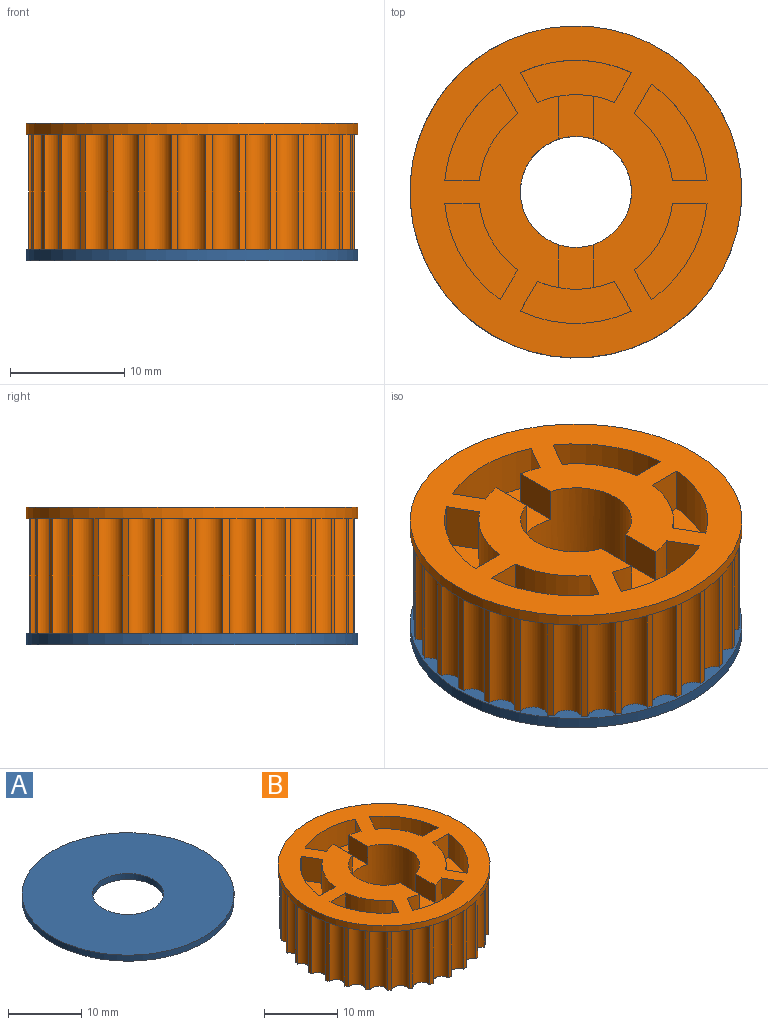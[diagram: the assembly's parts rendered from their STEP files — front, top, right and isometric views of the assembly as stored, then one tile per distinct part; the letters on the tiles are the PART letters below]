
ASSEMBLY  parts=2 mates=1
PART A: 4 faces, bbox 29x29x1 mm
  f0: cylinder r=14.5mm len=29mm, axis (0,0,-1), area 91.1mm2, adj f1,f2
  f1: plane 29x29mm, normal (0,0,1), area 586.6mm2, adj f0,f3
  f2: plane 29x29mm, normal (0,0,-1), area 586.6mm2, adj f0,f3
  f3: cylinder r=4.85mm len=9.7mm, axis (0,0,1), area 30.5mm2, adj f1,f2
PART B: 101 faces, bbox 29x29x11 mm
  f0: plane 28.5x28.4mm, normal (0,0,-1), area 510.3mm2, adj f1,f2,f3,f4,f5,f6,f7,f8
  f1: cylinder r=1.25mm len=10mm, axis (0,0,-1), area 33.2mm2, adj f0,f33,f35,f63
  f2: cylinder r=1.25mm len=10mm, axis (0,0,-1), area 33.2mm2, adj f0,f33,f62,f63
  f3: cylinder r=1.25mm len=10mm, axis (0,0,-1), area 33.2mm2, adj f0,f33,f61,f62
  f4: cylinder r=1.25mm len=10mm, axis (0,0,-1), area 33.2mm2, adj f0,f33,f60,f61
  f5: cylinder r=1.25mm len=10mm, axis (0,0,-1), area 33.2mm2, adj f0,f33,f59,f60
  f6: cylinder r=1.25mm len=10mm, axis (0,0,-1), area 33.2mm2, adj f0,f33,f58,f59
  f7: cylinder r=1.25mm len=10mm, axis (0,0,-1), area 33.2mm2, adj f0,f33,f57,f58
  f8: cylinder r=1.25mm len=10mm, axis (0,0,-1), area 33.2mm2, adj f0,f33,f56,f57
  f9: cylinder r=1.25mm len=10mm, axis (0,0,-1), area 33.2mm2, adj f0,f33,f55,f56
  f10: cylinder r=1.25mm len=10mm, axis (0,0,-1), area 33.2mm2, adj f0,f33,f54,f55
  f11: cylinder r=1.25mm len=10mm, axis (0,0,-1), area 33.2mm2, adj f0,f33,f53,f54
  f12: cylinder r=1.25mm len=10mm, axis (0,0,-1), area 33.2mm2, adj f0,f33,f52,f53
  f13: cylinder r=1.25mm len=10mm, axis (0,0,-1), area 33.2mm2, adj f0,f33,f51,f52
  f14: cylinder r=1.25mm len=10mm, axis (0,0,-1), area 33.2mm2, adj f0,f33,f50,f51
  f15: cylinder r=1.25mm len=10mm, axis (0,0,-1), area 33.2mm2, adj f0,f33,f49,f50
  f16: cylinder r=1.25mm len=10mm, axis (0,0,-1), area 33.2mm2, adj f0,f33,f48,f49
  f17: cylinder r=1.25mm len=10mm, axis (0,0,-1), area 33.2mm2, adj f0,f33,f47,f48
  f18: cylinder r=1.25mm len=10mm, axis (0,0,-1), area 33.2mm2, adj f0,f33,f46,f47
  f19: cylinder r=1.25mm len=10mm, axis (0,0,-1), area 33.2mm2, adj f0,f33,f45,f46
  f20: cylinder r=1.25mm len=10mm, axis (0,0,-1), area 33.2mm2, adj f0,f33,f44,f45
  f21: cylinder r=1.25mm len=10mm, axis (0,0,-1), area 33.2mm2, adj f0,f33,f43,f44
  f22: cylinder r=1.25mm len=10mm, axis (0,0,-1), area 33.2mm2, adj f0,f33,f42,f43
  f23: cylinder r=1.25mm len=10mm, axis (0,0,-1), area 33.2mm2, adj f0,f33,f41,f42
  f24: cylinder r=1.25mm len=10mm, axis (0,0,-1), area 33.2mm2, adj f0,f33,f40,f41
  f25: cylinder r=1.25mm len=10mm, axis (0,0,-1), area 33.2mm2, adj f0,f33,f39,f40
  f26: cylinder r=1.25mm len=10mm, axis (0,0,-1), area 33.2mm2, adj f0,f33,f38,f39
  f27: cylinder r=1.25mm len=10mm, axis (0,0,-1), area 33.2mm2, adj f0,f33,f37,f38
  f28: cylinder r=1.25mm len=10mm, axis (0,0,-1), area 33.2mm2, adj f0,f33,f36,f37
  f29: cylinder r=1.25mm len=10mm, axis (0,0,-1), area 33.2mm2, adj f0,f33,f34,f36
  f30: cylinder r=1.25mm len=10mm, axis (0,0,-1), area 33.2mm2, adj f0,f33,f34,f35
  f31: cylinder r=14.5mm len=29mm, axis (0,0,-1), area 91.1mm2, adj f32,f33
  f32: plane 29x29mm, normal (0,0,1), area 412.1mm2, adj f31,f64,f65,f66,f67,f69,f70,f71
  f33: plane 29x29mm, normal (0,0,-1), area 76.3mm2, adj f1,f2,f3,f4,f5,f6,f7,f8
  f34: cylinder r=14.25mm len=10mm, axis (0,0,-1), area 5.6mm2, adj f0,f29,f30,f33
  f35: cylinder r=14.25mm len=10mm, axis (0,0,-1), area 5.6mm2, adj f0,f1,f30,f33
  f36: cylinder r=14.25mm len=10mm, axis (0,0,-1), area 5.6mm2, adj f0,f28,f29,f33
  f37: cylinder r=14.25mm len=10mm, axis (0,0,-1), area 5.6mm2, adj f0,f27,f28,f33
  f38: cylinder r=14.25mm len=10mm, axis (0,0,-1), area 5.6mm2, adj f0,f26,f27,f33
  f39: cylinder r=14.25mm len=10mm, axis (0,0,-1), area 5.6mm2, adj f0,f25,f26,f33
  f40: cylinder r=14.25mm len=10mm, axis (0,0,-1), area 5.6mm2, adj f0,f24,f25,f33
  f41: cylinder r=14.25mm len=10mm, axis (0,0,-1), area 5.6mm2, adj f0,f23,f24,f33
  f42: cylinder r=14.25mm len=10mm, axis (0,0,-1), area 5.6mm2, adj f0,f22,f23,f33
  f43: cylinder r=14.25mm len=10mm, axis (0,0,-1), area 5.6mm2, adj f0,f21,f22,f33
  f44: cylinder r=14.25mm len=10mm, axis (0,0,-1), area 5.6mm2, adj f0,f20,f21,f33
  f45: cylinder r=14.25mm len=10mm, axis (0,0,-1), area 5.6mm2, adj f0,f19,f20,f33
  f46: cylinder r=14.25mm len=10mm, axis (0,0,-1), area 5.6mm2, adj f0,f18,f19,f33
  f47: cylinder r=14.25mm len=10mm, axis (0,0,-1), area 5.6mm2, adj f0,f17,f18,f33
  f48: cylinder r=14.25mm len=10mm, axis (0,0,-1), area 5.6mm2, adj f0,f16,f17,f33
  f49: cylinder r=14.25mm len=10mm, axis (0,0,-1), area 5.6mm2, adj f0,f15,f16,f33
  f50: cylinder r=14.25mm len=10mm, axis (0,0,-1), area 5.6mm2, adj f0,f14,f15,f33
  f51: cylinder r=14.25mm len=10mm, axis (0,0,-1), area 5.6mm2, adj f0,f13,f14,f33
  f52: cylinder r=14.25mm len=10mm, axis (0,0,-1), area 5.6mm2, adj f0,f12,f13,f33
  f53: cylinder r=14.25mm len=10mm, axis (0,0,-1), area 5.6mm2, adj f0,f11,f12,f33
  f54: cylinder r=14.25mm len=10mm, axis (0,0,-1), area 5.6mm2, adj f0,f10,f11,f33
  f55: cylinder r=14.25mm len=10mm, axis (0,0,-1), area 5.6mm2, adj f0,f9,f10,f33
  f56: cylinder r=14.25mm len=10mm, axis (0,0,-1), area 5.6mm2, adj f0,f8,f9,f33
  f57: cylinder r=14.25mm len=10mm, axis (0,0,-1), area 5.6mm2, adj f0,f7,f8,f33
  f58: cylinder r=14.25mm len=10mm, axis (0,0,-1), area 5.6mm2, adj f0,f6,f7,f33
  f59: cylinder r=14.25mm len=10mm, axis (0,0,-1), area 5.6mm2, adj f0,f5,f6,f33
  f60: cylinder r=14.25mm len=10mm, axis (0,0,-1), area 5.6mm2, adj f0,f4,f5,f33
  f61: cylinder r=14.25mm len=10mm, axis (0,0,-1), area 5.6mm2, adj f0,f3,f4,f33
  f62: cylinder r=14.25mm len=10mm, axis (0,0,-1), area 5.6mm2, adj f0,f2,f3,f33
  f63: cylinder r=14.25mm len=10mm, axis (0,0,-1), area 5.6mm2, adj f0,f1,f2,f33
  f64: cylinder r=11.5mm len=8.42mm, axis (0,0,1), area 40.2mm2, adj f32,f65,f67,f68
  f65: plane 4x3.02mm, normal (0,1,0), area 12.1mm2, adj f32,f64,f66,f68
  f66: cylinder r=8.5mm len=5.81mm, axis (0,0,1), area 27.6mm2, adj f32,f65,f67,f68
  f67: plane 4x2.61mm, normal (-0.87,-0.5,0), area 12.1mm2, adj f32,f64,f66,f68
  f68: plane 8.42x6.37mm, normal (0,0,1), area 25.4mm2, adj f64,f65,f66,f67
  f69: cylinder r=11.5mm len=8.42mm, axis (0,0,1), area 40.2mm2, adj f32,f70,f72,f73
  f70: plane 4x2.61mm, normal (-0.87,0.5,0), area 12.1mm2, adj f32,f69,f71,f73
  f71: cylinder r=8.5mm len=5.81mm, axis (0,0,1), area 27.6mm2, adj f32,f70,f72,f73
  f72: plane 4x3.02mm, normal (0,-1,0), area 12.1mm2, adj f32,f69,f71,f73
  f73: plane 8.42x6.37mm, normal (0,0,1), area 25.4mm2, adj f69,f70,f71,f72
  f74: cylinder r=11.5mm len=9.72mm, axis (0,0,1), area 40.2mm2, adj f32,f75,f77,f78
  f75: plane 4x2.61mm, normal (-0.87,-0.5,0), area 12.1mm2, adj f32,f74,f76,f78
  f76: cylinder r=8.5mm len=6.71mm, axis (0,0,1), area 18.5mm2, adj f32,f75,f77,f78,f98,f99,f100
  f77: plane 4x2.61mm, normal (0.87,-0.5,0), area 12.1mm2, adj f32,f74,f76,f78
  f78: plane 9.72x3.69mm, normal (0,0,1), area 25.4mm2, adj f74,f75,f76,f77
  f79: cylinder r=11.5mm len=8.42mm, axis (0,0,1), area 40.2mm2, adj f32,f80,f82,f83
  f80: plane 4x3.02mm, normal (0,-1,0), area 12.1mm2, adj f32,f79,f81,f83
  f81: cylinder r=8.5mm len=5.81mm, axis (0,0,1), area 27.6mm2, adj f32,f80,f82,f83
  f82: plane 4x2.61mm, normal (0.87,0.5,0), area 12.1mm2, adj f32,f79,f81,f83
  f83: plane 8.42x6.37mm, normal (0,0,1), area 25.4mm2, adj f79,f80,f81,f82
  f84: cylinder r=11.5mm len=8.42mm, axis (0,0,1), area 40.2mm2, adj f32,f85,f87,f88
  f85: plane 4x2.61mm, normal (0.87,-0.5,0), area 12.1mm2, adj f32,f84,f86,f88
  f86: cylinder r=8.5mm len=5.81mm, axis (0,0,1), area 27.6mm2, adj f32,f85,f87,f88
  f87: plane 4x3.02mm, normal (0,1,0), area 12.1mm2, adj f32,f84,f86,f88
  f88: plane 8.42x6.37mm, normal (0,0,1), area 25.4mm2, adj f84,f85,f86,f87
  f89: cylinder r=11.5mm len=9.72mm, axis (0,0,1), area 40.2mm2, adj f32,f90,f92,f93
  f90: plane 4x2.61mm, normal (0.87,0.5,0), area 12.1mm2, adj f32,f89,f91,f93
  f91: cylinder r=8.5mm len=6.71mm, axis (0,0,1), area 18.5mm2, adj f32,f90,f92,f93,f95,f96,f97
  f92: plane 4x2.61mm, normal (-0.87,0.5,0), area 12.1mm2, adj f32,f89,f91,f93
  f93: plane 9.72x3.69mm, normal (0,0,1), area 25.4mm2, adj f89,f90,f91,f92
  f94: cylinder r=4.85mm len=11mm, axis (0,0,1), area 316.9mm2, adj f0,f32,f95,f96,f97,f98,f99,f100
  f95: plane 3.89x3mm, normal (0,0,1), area 11.1mm2, adj f91,f94,f96,f97
  f96: plane 3.75x3mm, normal (-1,0,0), area 11.3mm2, adj f32,f91,f94,f95
  f97: plane 3.75x3mm, normal (1,0,0), area 11.3mm2, adj f32,f91,f94,f95
  f98: plane 3.75x3mm, normal (1,0,0), area 11.3mm2, adj f32,f76,f94,f100
  f99: plane 3.75x3mm, normal (-1,0,0), area 11.3mm2, adj f32,f76,f94,f100
  f100: plane 3.89x3mm, normal (0,0,1), area 11.1mm2, adj f76,f94,f98,f99
PLACE A t=(-15,6.11,16.16)mm
PLACE B t=(-15,6.11,16.16)mm
MATE fastened A.f0 <-> B.f34  axis (0,0,1) through (-15,6.11,17.16)mm
